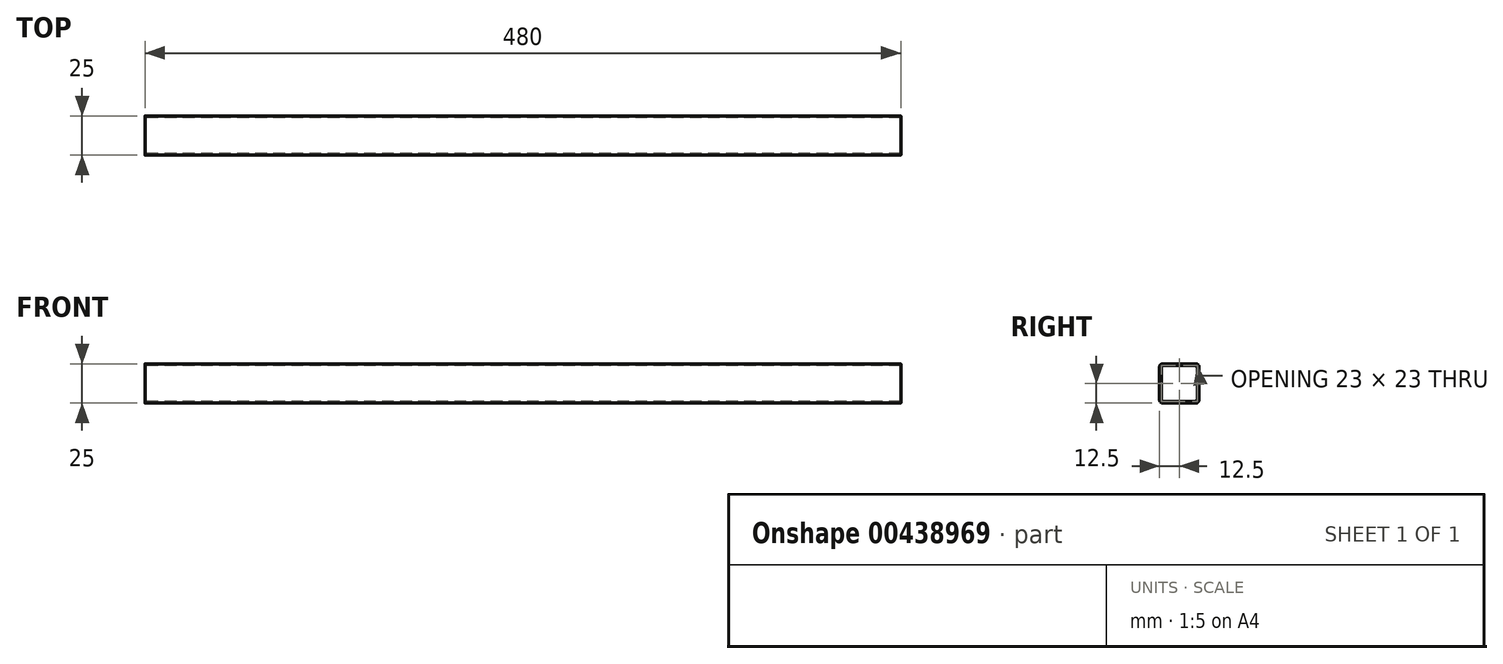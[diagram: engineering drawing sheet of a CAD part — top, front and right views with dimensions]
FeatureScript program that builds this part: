
annotation { "Feature Type Name" : "Feature", "Feature Type Description" : "" }
export const myFeature = defineFeature(function(context is Context, id is Id, definition is map)
    precondition{}
    {
        {
            var Q0;
            Q0=qCreatedBy(makeId("Right.planeOp"),FACE);
            var sketch = newSketch(context, id + "F0", { "sketchPlane" : qUnion([Q0])});
            skLineSegment(sketch, "E0.bottom", {"start": v(10.5, 12.5) * mm, "end": v(-10.5, 12.5) * mm});
            skLineSegment(sketch, "E0.top", {"start": v(10.5, -12.5) * mm, "end": v(-10.5, -12.5) * mm});
            skLineSegment(sketch, "E0.left", {"start": v(12.5, 10.5) * mm, "end": v(12.5, -10.5) * mm});
            skLineSegment(sketch, "E0.right", {"start": v(-12.5, 10.5) * mm, "end": v(-12.5, -10.5) * mm});
            skPoint(sketch, "E0.middle", {"position": v(0, 0) * mm});
            skLineSegment(sketch, "E1.bottom", {"start": v(9.5, 11.5) * mm, "end": v(-9.5, 11.5) * mm});
            skLineSegment(sketch, "E1.top", {"start": v(9.5, -11.5) * mm, "end": v(-9.5, -11.5) * mm});
            skLineSegment(sketch, "E1.left", {"start": v(11.5, 9.5) * mm, "end": v(11.5, -9.5) * mm});
            skLineSegment(sketch, "E1.right", {"start": v(-11.5, 9.5) * mm, "end": v(-11.5, -9.5) * mm});
            skPoint(sketch, "E2.visualSharp", {"position": v(-12.5, 12.5) * mm});
            skArc(sketch, "E2.filletArc", {"start": v(-10.5, 12.5) * mm, "mid": v(-11.91, 11.91) * mm, "end": v(-12.5, 10.5) * mm});
            skPoint(sketch, "E3.visualSharp", {"position": v(-11.5, 11.5) * mm});
            skArc(sketch, "E3.filletArc", {"start": v(-9.5, 11.5) * mm, "mid": v(-10.91, 10.91) * mm, "end": v(-11.5, 9.5) * mm});
            skPoint(sketch, "E4.visualSharp", {"position": v(12.5, 12.5) * mm});
            skArc(sketch, "E4.filletArc", {"start": v(12.5, 10.5) * mm, "mid": v(11.91, 11.91) * mm, "end": v(10.5, 12.5) * mm});
            skPoint(sketch, "E5.visualSharp", {"position": v(11.5, 11.5) * mm});
            skArc(sketch, "E5.filletArc", {"start": v(11.5, 9.5) * mm, "mid": v(10.91, 10.91) * mm, "end": v(9.5, 11.5) * mm});
            skPoint(sketch, "E6.visualSharp", {"position": v(12.5, -12.5) * mm});
            skArc(sketch, "E6.filletArc", {"start": v(10.5, -12.5) * mm, "mid": v(11.91, -11.91) * mm, "end": v(12.5, -10.5) * mm});
            skPoint(sketch, "E7.visualSharp", {"position": v(11.5, -11.5) * mm});
            skArc(sketch, "E7.filletArc", {"start": v(9.5, -11.5) * mm, "mid": v(10.91, -10.91) * mm, "end": v(11.5, -9.5) * mm});
            skPoint(sketch, "E8.visualSharp", {"position": v(-11.5, -11.5) * mm});
            skArc(sketch, "E8.filletArc", {"start": v(-11.5, -9.5) * mm, "mid": v(-10.91, -10.91) * mm, "end": v(-9.5, -11.5) * mm});
            skPoint(sketch, "E9.visualSharp", {"position": v(-12.5, -12.5) * mm});
            skArc(sketch, "E9.filletArc", {"start": v(-12.5, -10.5) * mm, "mid": v(-11.91, -11.91) * mm, "end": v(-10.5, -12.5) * mm});
            skSolve(sketch);
        }
        {
            var Q0;
            Q0=makeQuery(id+"F0.imprint","IMPRINT",FACE,{"disambiguationData":[TD([[makeQuery(id+"F0.imprint","IMPRINT",EDGE,{"derivedFrom":sQuery(id+"F0.wireOp",EDGE,"E0.bottom")}),1.0]])]});
            extrude(context, id + "F1", {"entities" : qUnion([Q0]), "endBound" : BoundingType.SYMMETRIC, "depth" : 480 * mm});
        }
    });
